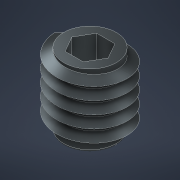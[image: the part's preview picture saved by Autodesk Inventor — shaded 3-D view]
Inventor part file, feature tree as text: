
AUTODESK INVENTOR PART (.ipt)
format: ipt  version: 2021 (Build 250183000, 183)  size: 256,000 bytes
history: native  units: mm
features: other x4, sketch x4, extrude x2, loft x1
ambient origin geometry x8: Origin, YZ Plane, XZ Plane, XY Plane, X Axis, Y Axis, Z Axis, Center Point
bodies: Body1 (feature_tree)
feature tree (11):
  other  "Sólido1"
  sketch  "Esboço1"  dims[d1=3.0mm d2=4.0mm d3=0.0mm]
  extrude  "Extrusão1"  Depth=4.0mm TaperAngle=0.0deg
  sketch  "Esboço2"  dims[d7=10.0mm d8=3.5mm d9=50.0mm d10=0.0mm d11=90.0deg d12=90.0deg d13=0.0mm d14=0.0mm d15=1.5mm d16=0.0mm]
  other  "Espiral1"
  extrude  "Extrusão2"  Depth=1.5mm TaperAngle=0.0deg
  other  "Plano de trabalho1"
  loft  "Transição1"
  sketch  "Esboço3"  dims[d17=0.2mm d18=2.5mm]
  sketch  "Esboço4"  dims[d19=10.0mm d20=90.0deg d21=0.0mm d22=90.0deg]
  other  "Arestas1"
